# Revit family: ACO AUS Gully 218 Fixed Height - Vertical Outlet - 300x300 topsize 4
name_source: partatom
category: Plumbing Fixtures
revit_build: Autodesk Revit 2014 (Build: 20130308_1515(x64)
units: mm (PartAtom-declared; Revit-internal decimal feet)

## types (8) — shared parameters
Fax = +61 (2) 4747 4029
Gully Colour = passivated stainless steel surface ( matt grey)
Gully Recyclable = Fully recyclable
Gully Recycled Material Content = 20 - 30 %
Gully Top Size (mm) = 300 x 300mm
Load Class = A15 - C250 (EN 1253) and D210 (AS 3996)
Manufacturer = ACO Polycrete
Price = POA - contact ACO
Product Range = ACO Gully 218
Product Type = Point Drainage
Telephone = +61 (2) 4747 4000
Water Mark 1 = This file is the property of ACO Passavant
Water Mark 2 = This file is water marked and users are prohibited to reproduce, adapt, distribute this information
Water Marked With = BIM Manager Premium Suite
Website = www.acoaus.com.au

## per-type parameters (varying)
- 142043 - Fixed Height without FAT-110mm Outlet-SS304: 110mm Dia Outlet=Yes; 160mm Dia Outlet=No; Flow Rate (l/s)=12.1; Foul Air Trap & Foul Air Trap Support Ring=No; Grating Product Code 408034=Load Class L15 (EN 1253) - Mesh grate - Slip Resistant - Stainless steel grade 304 - 268x268x25 - 2.1kg; Grating Product Code 408035=Load Class L15 (EN 1253) - Mesh grate - Plain - Stainless steel grade 304 - 268x268x25 - 2.1kg; Grating Product Code 408037=Load Class M125 (EN 1253) - Ladder grate - Slip Resistant - Stainless steel grade 304 - 168x168x25 - 4.3kg; Grating Product Code 408041=Load Class L15 (EN 1253) - Arla grate - Slip Resistant - Stainless steel grade 304 - 268x268x25 - 1.8kg; Grating Product Code 408045=Load Class D210 (EN 1253) - Ladder grate - Plain - Stainless steel grade 304 - 268x268x25 - 6.2kg; Grating product Code 142010=Load Class L15 (EN 1253) - 5 Star grate - Slip Resistant - Stainless steel grade 304 - 268x268x25 - 4.1kg; Grating product Code 416916=Load Class R50 (EN 1253) - Ladder grate - Slip Resistant - Stainless steel grade 304 - 268x268x25 - 3.5kg; Grating product Code 416944=Load Class M125 (EN 1253) - Cast grate - Slip Resistant - Stainless steel grade 304 - 168x168x25 - 5.6kg; Gully Depth=198 mm; Gully Material=Stainless steel grade 304; Gully Product Code=142043; Gully Product Description=ACO Gully 218 fixed height DN100 vertical outlet without Foul Air Trap - grade 304; Gully Top Opening=37.498 mm  [stored 0.123025 ft]; Gully Void Depth=-297 mm  [stored -0.974409 ft]; Material=Stainless Steel AISI 304; Outlet Depth=297 mm  [stored 0.974409 ft]; Outlet Diameter (mm)=110; Outlet Radius=55 mm  [stored 0.180446 ft]; Product Code 408223=0.7 litre removable strainer - Stainless steel grade 304 - 0.6kg; Product Code 413028=2.0 litre removable strainer - Stainless steel grade 304 - 0.9kg; Void Radius=55 mm  [stored 0.180446 ft]; Weight=3.5
- 142044 - Fixed Height without FAT-110mm Outlet-SS316: 110mm Dia Outlet=Yes; 160mm Dia Outlet=No; Flow Rate (l/s)=12.1; Foul Air Trap & Foul Air Trap Support Ring=No; Grating Product Code 408134=Load Class L15 (EN 1253) - Mesh grate -  Slip Resistant - Stainless steel grade 316 - 268x268x25 - 2.1kg; Grating Product Code 408135=Load Class L15 (EN 1253) - Mesh grate - Plain - Stainless steel grade 316 - 268x268x25 - 2.1kg; Grating Product Code 408141=Load Class L15 (EN 1253) - Arla grate -  Slip Resistant - Stainless steel grade 316 - 268x268x25 - 1.8kg; Grating product Code 408137=Load Class M125 (EN 1253) - Ladder grate -  Slip Resistant - Stainless steel grade 316 - 268x268x25 - 4.3kg; Grating product Code 408145=Load Class D210 (EN 1253) - Ladder grate - Plain - Stainless steel grade 316 - 268x268x25 - 6.2kg; Grating product Code 416917=Load Class R50 (EN 1253) - Ladder grate -  Slip Resistant - Stainless steel grade 316 - 268x268x25 - 3.5kg; Gully Depth=198 mm; Gully Material=Stainless steel grade 316; Gully Product Code=142044; Gully Product Description=ACO Gully 218 fixed height DN100 vertical outlet without Foul Air Trap - grade 316; Gully Top Opening=37.498 mm  [stored 0.123025 ft]; Gully Void Depth=-297 mm  [stored -0.974409 ft]; Material=Stainless Steel AISI 316; Outlet Depth=297 mm  [stored 0.974409 ft]; Outlet Diameter (mm)=110; Outlet Radius=55 mm  [stored 0.180446 ft]; Product Code 142001=Fixed strainer to suit a 110mm outlet - Stainless steel grade 316 - 0.1kg; Product Code 142003=Retention chain connecting fixed strainer to removable strainer - Stainless steel grade 316 - 0.1kg; Product Code 142005=Retention chain connecting removable strainer to grate - Stainless steel grade 316 - 0.1kg; Product Code 408233=0.7 litre removable strainer - Stainless steel grade 316 - 0.6kg; Product Code 413029=2.0 litre removable strainer - Stainless steel grade 316 - 0.9kg; Void Radius=55 mm  [stored 0.180446 ft]; Weight=3.5
- 142045 - Fixed Height with FAT-110mm Outlet-SS304: 110mm Dia Outlet=Yes; 160mm Dia Outlet=No; Flow Rate (l/s)=4.6; Foul Air Trap & Foul Air Trap Support Ring=Yes; Foul Air Trap Seal Colour=Black; Foul Air Trap Seal Material=NBR; Foul Air Trap Seal Recyclable=Fully recyclable; Foul Air Trap Seal Recycled Material Content=0%; Grating Product Code 408034=Load Class L15 (EN 1253) - Mesh grate - Slip Resistant - Stainless steel grade 304 - 268x268x25 - 2.1kg; Grating Product Code 408035=Load Class L15 (EN 1253) - Mesh grate - Plain - Stainless steel grade 304 - 268x268x25 - 2.1kg; Grating Product Code 408037=Load Class M125 (EN 1253) - Ladder grate - Slip Resistant - Stainless steel grade 304 - 168x168x25 - 4.3kg; Grating Product Code 408041=Load Class L15 (EN 1253) - Arla grate - Slip Resistant - Stainless steel grade 304 - 268x268x25 - 1.8kg; Grating Product Code 408045=Load Class D210 (EN 1253) - Ladder grate - Plain - Stainless steel grade 304 - 268x268x25 - 6.2kg; Grating product Code 142010=Load Class L15 (EN 1253) - 5 Star grate - Slip Resistant - Stainless steel grade 304 - 268x268x25 - 4.1kg; Grating product Code 416916=Load Class R50 (EN 1253) - Ladder grate - Slip Resistant - Stainless steel grade 304 - 268x268x25 - 3.5kg; Grating product Code 416944=Load Class M125 (EN 1253) - Cast grate - Slip Resistant - Stainless steel grade 304 - 168x168x25 - 5.6kg; Gully Depth=198 mm; Gully Material=Stainless steel grade 304; Gully Product Code=142045; Gully Product Description=ACO Gully 218 fixed height DN100 vertical outlet with Foul Air Trap - grade 304; Gully Top Opening=37.498 mm  [stored 0.123025 ft]; Gully Void Depth=-297 mm  [stored -0.974409 ft]; Material=Stainless Steel AISI 304; Outlet Depth=297 mm  [stored 0.974409 ft]; Outlet Diameter (mm)=110; Outlet Radius=55 mm  [stored 0.180446 ft]; Product Code 408223=0.7 litre removable strainer - Stainless steel grade 304 - 0.6kg; Product Code 413028=2.0 litre removable strainer - Stainless steel grade 304 - 0.9kg; Void Radius=55 mm  [stored 0.180446 ft]; Weight=4.5
- 142046 - Fixed Height with FAT-110mm Outlet-SS316: 110mm Dia Outlet=Yes; 160mm Dia Outlet=No; Flow Rate (l/s)=4.6; Foul Air Trap & Foul Air Trap Support Ring=Yes; Foul Air Trap Seal Colour=Black; Foul Air Trap Seal Material=NBR; Foul Air Trap Seal Recyclable=Fully recyclable; Foul Air Trap Seal Recycled Material Content=0%; Grating Product Code 408134=Load Class L15 (EN 1253) - Mesh grate -  Slip Resistant - Stainless steel grade 316 - 268x268x25 - 2.1kg; Grating Product Code 408135=Load Class L15 (EN 1253) - Mesh grate - Plain - Stainless steel grade 316 - 268x268x25 - 2.1kg; Grating Product Code 408141=Load Class L15 (EN 1253) - Arla grate -  Slip Resistant - Stainless steel grade 316 - 268x268x25 - 1.8kg; Grating product Code 408137=Load Class M125 (EN 1253) - Ladder grate -  Slip Resistant - Stainless steel grade 316 - 268x268x25 - 4.3kg; Grating product Code 408145=Load Class D210 (EN 1253) - Ladder grate - Plain - Stainless steel grade 316 - 268x268x25 - 6.2kg; Grating product Code 416917=Load Class R50 (EN 1253) - Ladder grate -  Slip Resistant - Stainless steel grade 316 - 268x268x25 - 3.5kg; Gully Depth=198 mm; Gully Material=Stainless steel grade 316; Gully Product Code=142046; Gully Product Description=ACO Gully 218 fixed height DN100 vertical outlet with Foul Air Trap - grade 316; Gully Top Opening=37.498 mm  [stored 0.123025 ft]; Gully Void Depth=-297 mm  [stored -0.974409 ft]; Material=Stainless Steel AISI 316; Outlet Depth=297 mm  [stored 0.974409 ft]; Outlet Diameter (mm)=110; Outlet Radius=55 mm  [stored 0.180446 ft]; Product Code 142001=Fixed strainer to suit a 110mm outlet - Stainless steel grade 316 - 0.1kg; Product Code 142002=Retention chain connecting fixed strainer to FAT - Stainless steel grade 316 - 0.1kg; Product Code 142003=Retention chain connecting fixed strainer to removable strainer - Stainless steel grade 316 - 0.1kg; Product Code 142004=Retention chain connecting to FAT  to removable strainer - Stainless steel grade 316 - 0.1kg; Product Code 142005=Retention chain connecting removable strainer to grate - Stainless steel grade 316 - 0.1kg; Product Code 142006=Retention chain connecting removable FAT to grate - Stainless steel grade 316 - 0.1kg; Product Code 408233=0.7 litre removable strainer - Stainless steel grade 316 - 0.6kg; Product Code 413029=2.0 litre removable strainer - Stainless steel grade 316 - 0.9kg; Void Radius=55 mm  [stored 0.180446 ft]; Weight=4.5
- 142047 - Fixed Height without FAT-160mm Outlet-SS304: 110mm Dia Outlet=No; 160mm Dia Outlet=Yes; Flow Rate (l/s)=25.8; Foul Air Trap & Foul Air Trap Support Ring=No; Grating Product Code 408034=Load Class L15 (EN 1253) - Mesh grate - Slip Resistant - Stainless steel grade 304 - 268x268x25 - 2.1kg; Grating Product Code 408035=Load Class L15 (EN 1253) - Mesh grate - Plain - Stainless steel grade 304 - 268x268x25 - 2.1kg; Grating Product Code 408037=Load Class M125 (EN 1253) - Ladder grate - Slip Resistant - Stainless steel grade 304 - 168x168x25 - 4.3kg; Grating Product Code 408041=Load Class L15 (EN 1253) - Arla grate - Slip Resistant - Stainless steel grade 304 - 268x268x25 - 1.8kg; Grating Product Code 408045=Load Class D210 (EN 1253) - Ladder grate - Plain - Stainless steel grade 304 - 268x268x25 - 6.2kg; Grating product Code 142010=Load Class L15 (EN 1253) - 5 Star grate - Slip Resistant - Stainless steel grade 304 - 268x268x25 - 4.1kg; Grating product Code 416916=Load Class R50 (EN 1253) - Ladder grate - Slip Resistant - Stainless steel grade 304 - 268x268x25 - 3.5kg; Grating product Code 416944=Load Class M125 (EN 1253) - Cast grate - Slip Resistant - Stainless steel grade 304 - 168x168x25 - 5.6kg; Gully Depth=200 mm  [stored 0.656168 ft]; Gully Material=Stainless steel grade 304; Gully Product Code=142047; Gully Product Description=ACO Gully 218 fixed height DN150 vertical outlet without Foul Air Trap - grade 304; Gully Top Opening=12.594 mm  [stored 0.0413189 ft]; Gully Void Depth=-275 mm; Material=Stainless Steel AISI 304; Outlet Depth=275 mm; Outlet Diameter (mm)=160; Outlet Radius=80 mm  [stored 0.262467 ft]; Product Code 408223=0.7 litre removable strainer - Stainless steel grade 304 - 0.6kg; Product Code 413028=2.0 litre removable strainer - Stainless steel grade 304 - 0.9kg; Void Radius=80 mm  [stored 0.262467 ft]; Weight=3.4
- 142048 - Fixed Height without FAT-160mm Outlet-SS316: 110mm Dia Outlet=No; 160mm Dia Outlet=Yes; Flow Rate (l/s)=25.8; Foul Air Trap & Foul Air Trap Support Ring=No; Grating Product Code 408134=Load Class L15 (EN 1253) - Mesh grate -  Slip Resistant - Stainless steel grade 316 - 268x268x25 - 2.1kg; Grating Product Code 408135=Load Class L15 (EN 1253) - Mesh grate - Plain - Stainless steel grade 316 - 268x268x25 - 2.1kg; Grating Product Code 408141=Load Class L15 (EN 1253) - Arla grate -  Slip Resistant - Stainless steel grade 316 - 268x268x25 - 1.8kg; Grating product Code 408137=Load Class M125 (EN 1253) - Ladder grate -  Slip Resistant - Stainless steel grade 316 - 268x268x25 - 4.3kg; Grating product Code 408145=Load Class D210 (EN 1253) - Ladder grate - Plain - Stainless steel grade 316 - 268x268x25 - 6.2kg; Grating product Code 416917=Load Class R50 (EN 1253) - Ladder grate -  Slip Resistant - Stainless steel grade 316 - 268x268x25 - 3.5kg; Gully Depth=200 mm  [stored 0.656168 ft]; Gully Material=Stainless steel grade 316; Gully Product Code=142048; Gully Product Description=ACO Gully 218 fixed height DN150 vertical outlet without Foul Air Trap - grade 316; Gully Top Opening=12.594 mm  [stored 0.0413189 ft]; Gully Void Depth=-275 mm; Material=Stainless Steel AISI 316; Outlet Depth=275 mm; Outlet Diameter (mm)=160; Outlet Radius=80 mm  [stored 0.262467 ft]; Product Code 142003=Retention chain connecting fixed strainer to removable strainer - Stainless steel grade 316 - 0.1kg; Product Code 142005=Retention chain connecting removable strainer to grate - Stainless steel grade 316 - 0.1kg; Product Code 142008=Fixed strainer to suit a 160mm outlet - Stainless steel grade 316 - 0.1kg; Product Code 408233=0.7 litre removable strainer - Stainless steel grade 316 - 0.6kg; Product Code 413029=2.0 litre removable strainer - Stainless steel grade 316 - 0.9kg; Void Radius=80 mm  [stored 0.262467 ft]; Weight=3.4
- 142049 - Fixed Height with FAT-160mm Outlet-SS304: 110mm Dia Outlet=No; 160mm Dia Outlet=Yes; Flow Rate (l/s)=4.6; Foul Air Trap & Foul Air Trap Support Ring=Yes; Foul Air Trap Seal Colour=Black; Foul Air Trap Seal Material=NBR; Foul Air Trap Seal Recyclable=Fully recyclable; Foul Air Trap Seal Recycled Material Content=0%; Grating Product Code 408034=Load Class L15 (EN 1253) - Mesh grate - Slip Resistant - Stainless steel grade 304 - 268x268x25 - 2.1kg; Grating Product Code 408035=Load Class L15 (EN 1253) - Mesh grate - Plain - Stainless steel grade 304 - 268x268x25 - 2.1kg; Grating Product Code 408037=Load Class M125 (EN 1253) - Ladder grate - Slip Resistant - Stainless steel grade 304 - 168x168x25 - 4.3kg; Grating Product Code 408041=Load Class L15 (EN 1253) - Arla grate - Slip Resistant - Stainless steel grade 304 - 268x268x25 - 1.8kg; Grating Product Code 408045=Load Class D210 (EN 1253) - Ladder grate - Plain - Stainless steel grade 304 - 268x268x25 - 6.2kg; Grating product Code 142010=Load Class L15 (EN 1253) - 5 Star grate - Slip Resistant - Stainless steel grade 304 - 268x268x25 - 4.1kg; Grating product Code 416916=Load Class R50 (EN 1253) - Ladder grate - Slip Resistant - Stainless steel grade 304 - 268x268x25 - 3.5kg; Grating product Code 416944=Load Class M125 (EN 1253) - Cast grate - Slip Resistant - Stainless steel grade 304 - 168x168x25 - 5.6kg; Gully Depth=200 mm  [stored 0.656168 ft]; Gully Material=Stainless steel grade 304; Gully Product Code=142049; Gully Product Description=ACO Gully 218 fixed height DN150 vertical outlet with Foul Air Trap - grade 304; Gully Top Opening=12.594 mm  [stored 0.0413189 ft]; Gully Void Depth=-275 mm; Material=Stainless Steel AISI 304; Outlet Depth=275 mm; Outlet Diameter (mm)=160; Outlet Radius=80 mm  [stored 0.262467 ft]; Product Code 408223=0.7 litre removable strainer - Stainless steel grade 304 - 0.6kg; Product Code 413028=2.0 litre removable strainer - Stainless steel grade 304 - 0.9kg; Void Radius=80 mm  [stored 0.262467 ft]; Weight=4.4
- 142050 - Fixed Height with FAT-160mm Outlet-SS316: 110mm Dia Outlet=No; 160mm Dia Outlet=Yes; Flow Rate (l/s)=4.6; Foul Air Trap & Foul Air Trap Support Ring=Yes; Foul Air Trap Seal Colour=Black; Foul Air Trap Seal Material=NBR; Foul Air Trap Seal Recyclable=Fully recyclable; Foul Air Trap Seal Recycled Material Content=0%; Grating Product Code 408134=Load Class L15 (EN 1253) - Mesh grate -  Slip Resistant - Stainless steel grade 316 - 268x268x25 - 2.1kg; Grating Product Code 408135=Load Class L15 (EN 1253) - Mesh grate - Plain - Stainless steel grade 316 - 268x268x25 - 2.1kg; Grating Product Code 408141=Load Class L15 (EN 1253) - Arla grate -  Slip Resistant - Stainless steel grade 316 - 268x268x25 - 1.8kg; Grating product Code 408137=Load Class M125 (EN 1253) - Ladder grate -  Slip Resistant - Stainless steel grade 316 - 268x268x25 - 4.3kg; Grating product Code 408145=Load Class D210 (EN 1253) - Ladder grate - Plain - Stainless steel grade 316 - 268x268x25 - 6.2kg; Grating product Code 416917=Load Class R50 (EN 1253) - Ladder grate -  Slip Resistant - Stainless steel grade 316 - 268x268x25 - 3.5kg; Gully Depth=200 mm  [stored 0.656168 ft]; Gully Material=Stainless steel grade 316; Gully Product Code=142050; Gully Product Description=ACO Gully 218 fixed height DN150 vertical outlet with Foul Air Trap - grade 316; Gully Top Opening=12.594 mm  [stored 0.0413189 ft]; Gully Void Depth=-275 mm; Material=Stainless Steel AISI 316; Outlet Depth=275 mm; Outlet Diameter (mm)=160; Outlet Radius=80 mm  [stored 0.262467 ft]; Product Code 142002=Retention chain connecting fixed strainer to FAT - Stainless steel grade 316 - 0.1kg; Product Code 142003=Retention chain connecting fixed strainer to removable strainer - Stainless steel grade 316 - 0.1kg; Product Code 142004=Retention chain connecting to FAT  to removable strainer - Stainless steel grade 316 - 0.1kg; Product Code 142005=Retention chain connecting removable strainer to grate - Stainless steel grade 316 - 0.1kg; Product Code 142006=Retention chain connecting removable FAT to grate - Stainless steel grade 316 - 0.1kg; Product Code 142008=Fixed strainer to suit a 160mm outlet - Stainless steel grade 316 - 0.1kg; Product Code 408233=0.7 litre removable strainer - Stainless steel grade 316 - 0.6kg; Product Code 413029=2.0 litre removable strainer - Stainless steel grade 316 - 0.9kg; Void Radius=80 mm  [stored 0.262467 ft]; Weight=4.4

note: [stored X ft] marks values corroborated as IEEE doubles in the binary element streams (Revit-internal decimal feet)

## geometry (parser evidence)
native form markers: Blend x2, Sweep x2
no freeform markers — native parametric forms only
